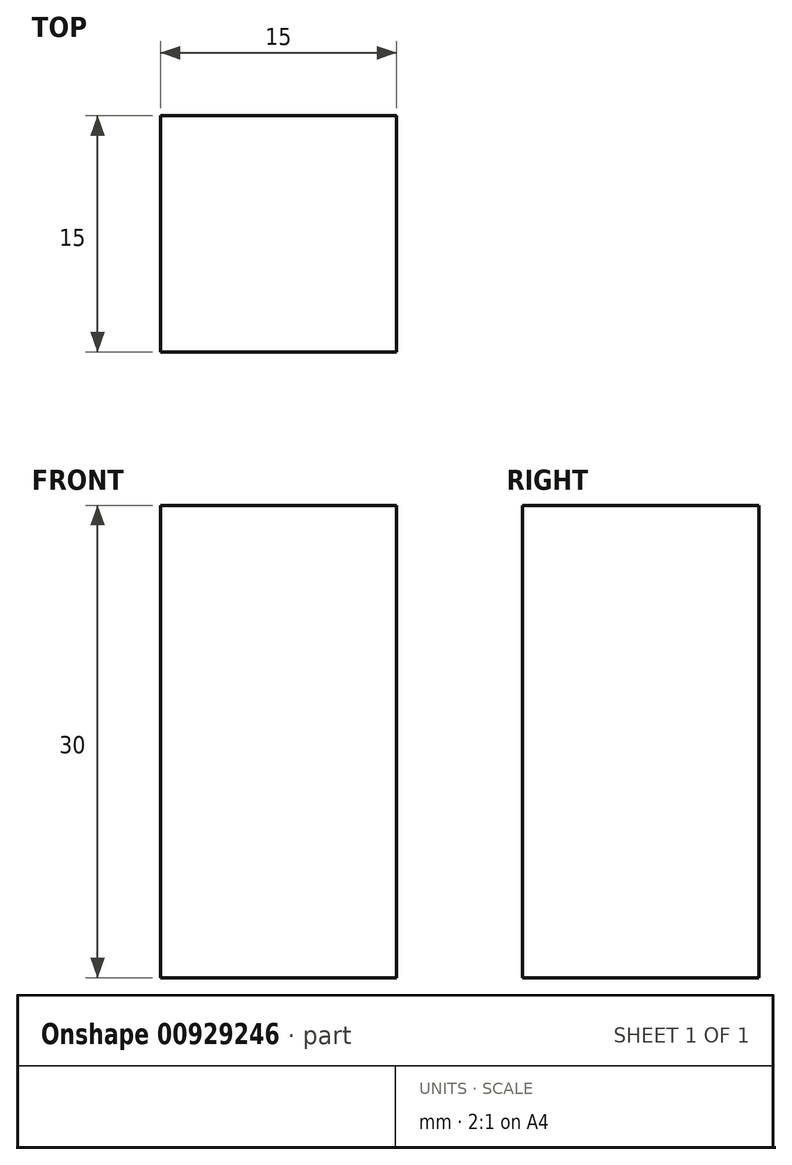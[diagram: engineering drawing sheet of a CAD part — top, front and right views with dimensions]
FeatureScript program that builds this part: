
annotation { "Feature Type Name" : "Feature", "Feature Type Description" : "" }
export const myFeature = defineFeature(function(context is Context, id is Id, definition is map)
    precondition{}
    {
        {
            var Q0;
            Q0=qCreatedBy(makeId("Top.planeOp"),FACE);
            var sketch = newSketch(context, id + "F0", { "sketchPlane" : qUnion([Q0])});
            skLineSegment(sketch, "E0.bottom", {"start": v(7.5, -7.5) * mm, "end": v(-7.5, -7.5) * mm});
            skLineSegment(sketch, "E0.top", {"start": v(7.5, 7.5) * mm, "end": v(-7.5, 7.5) * mm});
            skLineSegment(sketch, "E0.left", {"start": v(7.5, -7.5) * mm, "end": v(7.5, 7.5) * mm});
            skLineSegment(sketch, "E0.right", {"start": v(-7.5, -7.5) * mm, "end": v(-7.5, 7.5) * mm});
            skPoint(sketch, "E0.middle", {"position": v(0, 0) * mm});
            skSolve(sketch);
        }
        {
            var Q0;
            Q0 = qSketchRegion(id + "F0", true);
            extrude(context, id + "F1", {"entities" : qUnion([Q0]), "depth" : 30 * mm, "offsetDistance" : 25 * mm});
        }
    });
